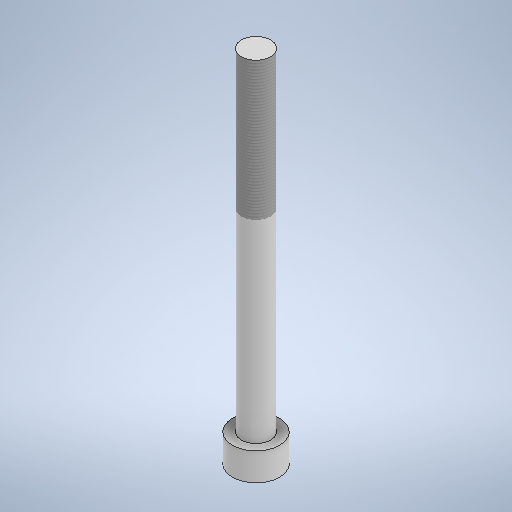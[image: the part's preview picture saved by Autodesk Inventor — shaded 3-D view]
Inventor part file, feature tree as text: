
AUTODESK INVENTOR PART (.ipt)
format: ipt  version: 2025.2 (Build 292293000, 293)  size: 250,880 bytes
history: native  units: mm
features: extrude x2, sketch x2, other x1, thread x1
ambient origin geometry x8: Origin, YZ Plane, XZ Plane, XY Plane, X Axis, Y Axis, Z Axis, Center Point
bodies: Body1 (feature_tree)
feature tree (6):
  other  "Bryła1"
  extrude  "Wyciągnięcie proste1"  Depth=8.5mm
  extrude  "Wyciągnięcie proste2"  Depth=5.0mm TaperAngle=0.0deg
  thread  "Gwint1"
  sketch  "Szkic1"
  sketch  "Szkic2"
